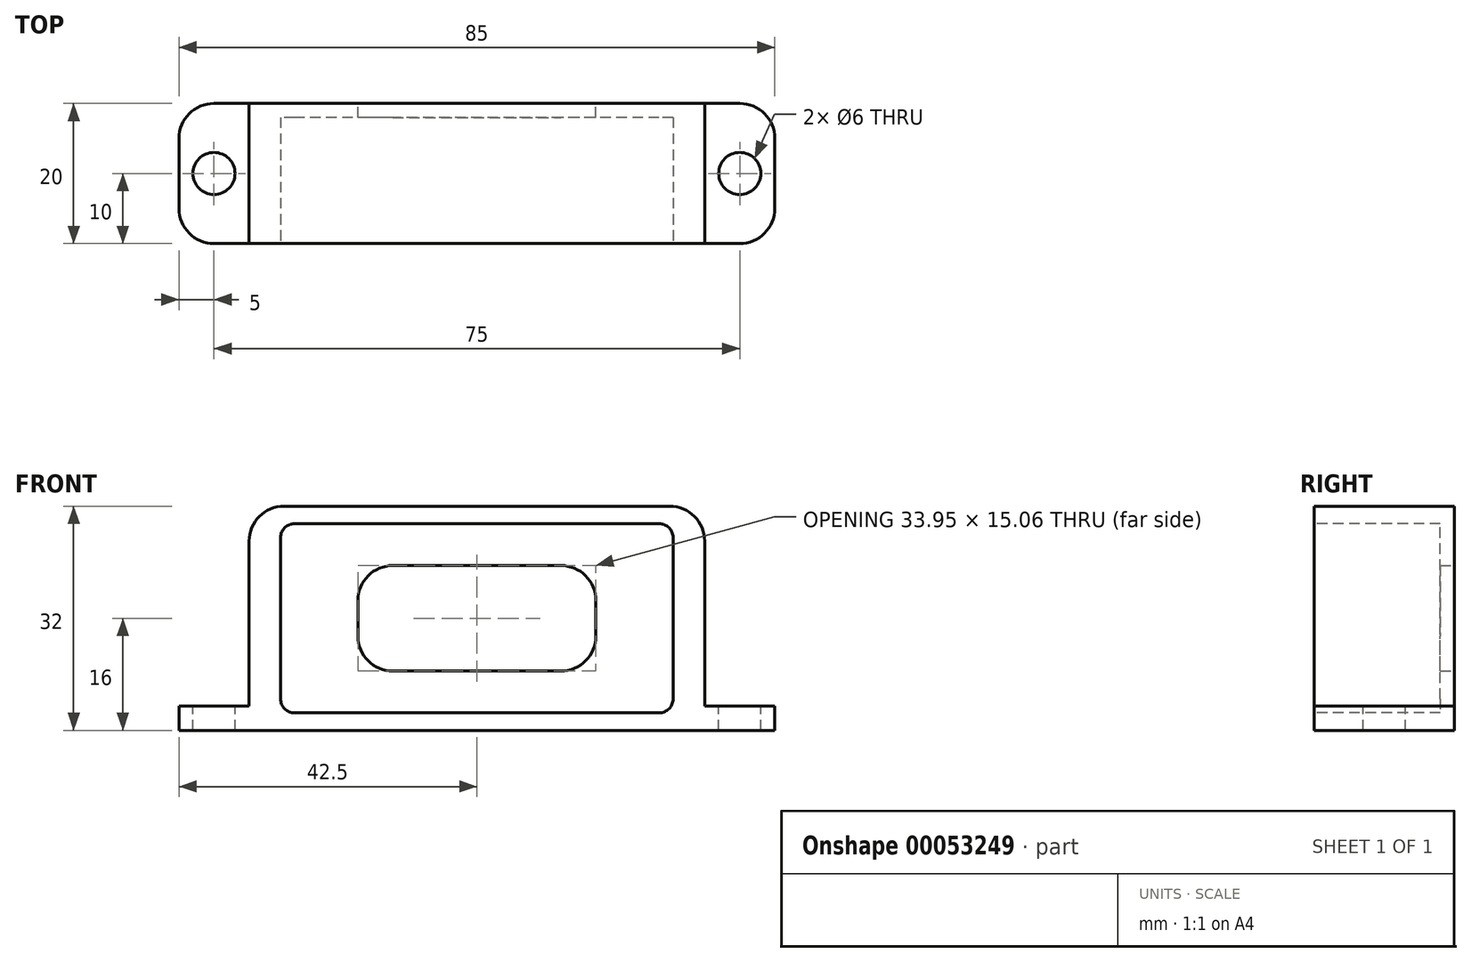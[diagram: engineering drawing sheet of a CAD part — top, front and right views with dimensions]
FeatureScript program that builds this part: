
annotation { "Feature Type Name" : "Feature", "Feature Type Description" : "" }
export const myFeature = defineFeature(function(context is Context, id is Id, definition is map)
    precondition{}
    {
        {
            var Q0;
            Q0=qCreatedBy(makeId("Front.planeOp"),FACE);
            var sketch = newSketch(context, id + "F0", { "sketchPlane" : qUnion([Q0])});
            skLineSegment(sketch, "E0.bottom", {"start": v(0, 0) * mm, "end": v(-65, 0) * mm});
            skLineSegment(sketch, "E0.top", {"start": v(0, 32) * mm, "end": v(-65, 32) * mm});
            skLineSegment(sketch, "E0.left", {"start": v(0, 0) * mm, "end": v(0, 32) * mm});
            skLineSegment(sketch, "E0.right", {"start": v(-65, 0) * mm, "end": v(-65, 32) * mm});
            skLineSegment(sketch, "E1.bottom", {"start": v(-65, 0) * mm, "end": v(-75, 0) * mm});
            skLineSegment(sketch, "E1.top", {"start": v(-65, 3.5) * mm, "end": v(-75, 3.5) * mm});
            skLineSegment(sketch, "E1.left", {"start": v(-65, 0) * mm, "end": v(-65, 3.5) * mm});
            skLineSegment(sketch, "E1.right", {"start": v(-75, 0) * mm, "end": v(-75, 3.5) * mm});
            skPoint(sketch, "E2.oppositeSnap0", {"position": v(-70, 3.5) * mm});
            skLineSegment(sketch, "E2.bottom", {"start": v(0, 0) * mm, "end": v(10, 0) * mm});
            skLineSegment(sketch, "E2.top", {"start": v(0, 3.5) * mm, "end": v(10, 3.5) * mm});
            skLineSegment(sketch, "E2.left", {"start": v(0, 0) * mm, "end": v(0, 3.5) * mm});
            skLineSegment(sketch, "E2.right", {"start": v(10, 0) * mm, "end": v(10, 3.5) * mm});
            skSolve(sketch);
        }
        {
            var Q0;
            Q0=makeQuery(id+"F0.imprint","IMPRINT",FACE,{"disambiguationData":[TD([[makeQuery(id+"F0.imprint","IMPRINT",EDGE,{"derivedFrom":sQuery(id+"F0.wireOp",EDGE,"E1.bottom")}),-1.0]])]});
            var Q1;
            Q1=makeQuery(id+"F0.imprint","IMPRINT",FACE,{"disambiguationData":[TD([[makeQuery(id+"F0.imprint","IMPRINT",EDGE,{"derivedFrom":sQuery(id+"F0.wireOp",EDGE,"E0.bottom")}),-1.0]])]});
            var Q2;
            Q2=makeQuery(id+"F0.imprint","IMPRINT",FACE,{"disambiguationData":[TD([[makeQuery(id+"F0.imprint","IMPRINT",EDGE,{"derivedFrom":sQuery(id+"F0.wireOp",EDGE,"E2.bottom")}),1.0]])]});
            extrude(context, id + "F1", {"entities" : qUnion([Q0, Q1, Q2]), "depth" : 20 * mm});
        }
        {
            var Q0;
            Q0=makeQuery(id+"F1.opExtrude","SWEPT_FACE",FACE,{"disambiguationData":[OSD([sQuery(id+"F0.wireOp",EDGE,"E2.top")])]});
            var sketch = newSketch(context, id + "F2", { "sketchPlane" : qUnion([Q0])});
            skLineSegment(sketch, "E3", {"start": v(0, -10) * mm, "end": v(10, -10) * mm, "construction": true});
            skCircle(sketch, "E4", {"center": v(5, -10) * mm, "radius": 3 * mm});
            skSolve(sketch);
        }
        {
            var Q0;
            Q0=makeQuery(id+"F2.imprint","IMPRINT",FACE,{"disambiguationData":[TD([[makeQuery(id+"F2.imprint","IMPRINT",EDGE,{"derivedFrom":sQuery(id+"F2.wireOp",EDGE,"E4")}),1.0]])]});
            extrude(context, id + "F3", {"entities" : qUnion([Q0]), "operationType" : NewBodyOperationType.REMOVE, "endBound" : BoundingType.THROUGH_ALL, "oppositeDirection" : true, "depth" : 25 * mm});
        }
        {
            var Q0;
            Q0=qCreatedBy(makeId("Right.planeOp"),FACE);
            cPlane(context, id + "F4", {"entities" : qUnion([Q0]), "cplaneType" : CPlaneType.OFFSET, "offset" : (65 / 2) * mm, "oppositeDirection" : true, "width" : 150 * mm, "height" : 150 * mm});
        }
        {
            var Q0;
            Q0=makeQuery(id+"F3.boolean.opBoolean","COPY",FACE,{"derivedFrom":makeQuery(id+"F3.opExtrude","SWEPT_FACE",FACE,{"disambiguationData":[OSD([sQuery(id+"F2.wireOp",EDGE,"E4")])]})});
            var Q1;
            Q1=qCreatedBy(id+"F4.planeOp",FACE);
            mirror(context, id + "F5", {"faces" : qUnion([Q0]), "mirrorPlane" : qUnion([Q1]), "patternType" : MirrorType.FACE});
        }
        {
            var Q0;
            Q0=makeQuery(id+"F1.opExtrude","SWEPT_EDGE",EDGE,{"disambiguationData":[OSD([sQuery(id+"F0.wireOp",EDGE,"E0.top"),sQuery(id+"F0.wireOp",EDGE,"E0.left")])]});
            var Q1;
            Q1=makeQuery(id+"F1.opExtrude","SWEPT_EDGE",EDGE,{"disambiguationData":[OSD([sQuery(id+"F0.wireOp",EDGE,"E0.top"),sQuery(id+"F0.wireOp",EDGE,"E0.right")])]});
            fillet(context, id + "F6", {"entities" : qUnion([Q0, Q1]), "radius" : 5 * mm, "tangentPropagation" : true, "allowEdgeOverflow" : false});
        }
        {
            var Q0;
            Q0=makeQuery(id+"F1.opExtrude","CAP_FACE",FACE,{"disambiguationData":[OSD([sQuery(id+"F0.wireOp",EDGE,"E0.bottom"),sQuery(id+"F0.wireOp",EDGE,"E0.top"),sQuery(id+"F0.wireOp",EDGE,"E0.left"),sQuery(id+"F0.wireOp",EDGE,"E0.right"),sQuery(id+"F0.wireOp",EDGE,"E1.bottom"),sQuery(id+"F0.wireOp",EDGE,"E1.top"),sQuery(id+"F0.wireOp",EDGE,"E1.right"),sQuery(id+"F0.wireOp",EDGE,"E2.bottom"),sQuery(id+"F0.wireOp",EDGE,"E2.top"),sQuery(id+"F0.wireOp",EDGE,"E2.right")])],"isStart":true});
            var sketch = newSketch(context, id + "F7", { "sketchPlane" : qUnion([Q0])});
            skLineSegment(sketch, "E5", {"start": v(32.5, 32) * mm, "end": v(32.5, 0) * mm, "construction": true});
            skLineSegment(sketch, "E6", {"start": v(32.5, 16) * mm, "end": v(10.72, 16) * mm, "construction": true});
            skLineSegment(sketch, "E7.rect.bottom", {"start": v(20.53, 8.47) * mm, "end": v(44.47, 8.47) * mm});
            skLineSegment(sketch, "E7.rect.top", {"start": v(20.53, 23.53) * mm, "end": v(44.47, 23.53) * mm});
            skLineSegment(sketch, "E7.rect.left", {"start": v(15.53, 13.47) * mm, "end": v(15.53, 18.53) * mm});
            skLineSegment(sketch, "E7.rect.right", {"start": v(49.47, 13.47) * mm, "end": v(49.47, 18.53) * mm});
            skPoint(sketch, "E7.rect.middle", {"position": v(32.5, 16) * mm});
            skPoint(sketch, "E8.visualSharp", {"position": v(15.53, 23.53) * mm});
            skArc(sketch, "E8.filletArc", {"start": v(20.53, 23.53) * mm, "mid": v(16.99, 22.07) * mm, "end": v(15.53, 18.53) * mm});
            skPoint(sketch, "E9.visualSharp", {"position": v(49.47, 23.53) * mm});
            skArc(sketch, "E9.filletArc", {"start": v(49.47, 18.53) * mm, "mid": v(48.01, 22.07) * mm, "end": v(44.47, 23.53) * mm});
            skPoint(sketch, "E10.visualSharp", {"position": v(49.47, 8.47) * mm});
            skArc(sketch, "E10.filletArc", {"start": v(44.47, 8.47) * mm, "mid": v(48.01, 9.93) * mm, "end": v(49.47, 13.47) * mm});
            skPoint(sketch, "E11.visualSharp", {"position": v(15.53, 8.47) * mm});
            skArc(sketch, "E11.filletArc", {"start": v(15.53, 13.47) * mm, "mid": v(16.99, 9.93) * mm, "end": v(20.53, 8.47) * mm});
            skSolve(sketch);
        }
        {
            var Q0;
            Q0=makeQuery(id+"F1.opExtrude","CAP_FACE",FACE,{"disambiguationData":[OSD([sQuery(id+"F0.wireOp",EDGE,"E0.bottom"),sQuery(id+"F0.wireOp",EDGE,"E0.top"),sQuery(id+"F0.wireOp",EDGE,"E0.left"),sQuery(id+"F0.wireOp",EDGE,"E0.right"),sQuery(id+"F0.wireOp",EDGE,"E1.bottom"),sQuery(id+"F0.wireOp",EDGE,"E1.top"),sQuery(id+"F0.wireOp",EDGE,"E1.right"),sQuery(id+"F0.wireOp",EDGE,"E2.bottom"),sQuery(id+"F0.wireOp",EDGE,"E2.top"),sQuery(id+"F0.wireOp",EDGE,"E2.right")])],"isStart":false});
            var sketch = newSketch(context, id + "F8", { "sketchPlane" : qUnion([Q0])});
            skPoint(sketch, "E12.0", {"position": v(-32.5, 16) * mm});
            skLineSegment(sketch, "E13.rect.bottom", {"start": v(-6.5, 2.5) * mm, "end": v(-58.5, 2.5) * mm});
            skLineSegment(sketch, "E13.rect.top", {"start": v(-6.5, 29.5) * mm, "end": v(-58.5, 29.5) * mm});
            skLineSegment(sketch, "E13.rect.left", {"start": v(-4.5, 4.5) * mm, "end": v(-4.5, 27.5) * mm});
            skLineSegment(sketch, "E13.rect.right", {"start": v(-60.5, 4.5) * mm, "end": v(-60.5, 27.5) * mm});
            skPoint(sketch, "E14.visualSharp", {"position": v(-60.5, 29.5) * mm});
            skArc(sketch, "E14.filletArc", {"start": v(-58.5, 29.5) * mm, "mid": v(-59.91, 28.91) * mm, "end": v(-60.5, 27.5) * mm});
            skPoint(sketch, "E15.visualSharp", {"position": v(-4.5, 29.5) * mm});
            skArc(sketch, "E15.filletArc", {"start": v(-4.5, 27.5) * mm, "mid": v(-5.09, 28.91) * mm, "end": v(-6.5, 29.5) * mm});
            skPoint(sketch, "E16.visualSharp", {"position": v(-4.5, 2.5) * mm});
            skArc(sketch, "E16.filletArc", {"start": v(-6.5, 2.5) * mm, "mid": v(-5.09, 3.09) * mm, "end": v(-4.5, 4.5) * mm});
            skPoint(sketch, "E17.visualSharp", {"position": v(-60.5, 2.5) * mm});
            skArc(sketch, "E17.filletArc", {"start": v(-60.5, 4.5) * mm, "mid": v(-59.91, 3.09) * mm, "end": v(-58.5, 2.5) * mm});
            skSolve(sketch);
        }
        {
            var Q0;
            Q0=makeQuery(id+"F8.imprint","IMPRINT",FACE,{"disambiguationData":[TD([[makeQuery(id+"F8.imprint","IMPRINT",EDGE,{"derivedFrom":sQuery(id+"F8.wireOp",EDGE,"E13.rect.bottom")}),-1.0]])]});
            extrude(context, id + "F9", {"entities" : qUnion([Q0]), "operationType" : NewBodyOperationType.REMOVE, "oppositeDirection" : true, "depth" : 18 * mm});
        }
        {
            var Q0;
            Q0=makeQuery(id+"F7.imprint","IMPRINT",FACE,{"disambiguationData":[TD([[makeQuery(id+"F7.imprint","IMPRINT",EDGE,{"derivedFrom":sQuery(id+"F7.wireOp",EDGE,"E7.rect.bottom")}),1.0]])]});
            extrude(context, id + "F10", {"entities" : qUnion([Q0]), "operationType" : NewBodyOperationType.REMOVE, "endBound" : BoundingType.THROUGH_ALL, "oppositeDirection" : true, "depth" : 25 * mm});
        }
        {
            var Q0;
            Q0=makeQuery(id+"F1.opExtrude","CAP_EDGE",EDGE,{"disambiguationData":[OSD([sQuery(id+"F0.wireOp",EDGE,"E1.right")])],"isStart":false});
            var Q1;
            Q1=makeQuery(id+"F1.opExtrude","CAP_EDGE",EDGE,{"disambiguationData":[OSD([sQuery(id+"F0.wireOp",EDGE,"E1.right")])],"isStart":true});
            var Q2;
            Q2=makeQuery(id+"F1.opExtrude","CAP_EDGE",EDGE,{"disambiguationData":[OSD([sQuery(id+"F0.wireOp",EDGE,"E2.right")])],"isStart":false});
            var Q3;
            Q3=makeQuery(id+"F1.opExtrude","CAP_EDGE",EDGE,{"disambiguationData":[OSD([sQuery(id+"F0.wireOp",EDGE,"E2.right")])],"isStart":true});
            fillet(context, id + "F11", {"entities" : qUnion([Q0, Q1, Q2, Q3]), "radius" : 5 * mm, "tangentPropagation" : true, "allowEdgeOverflow" : false});
        }
    });
